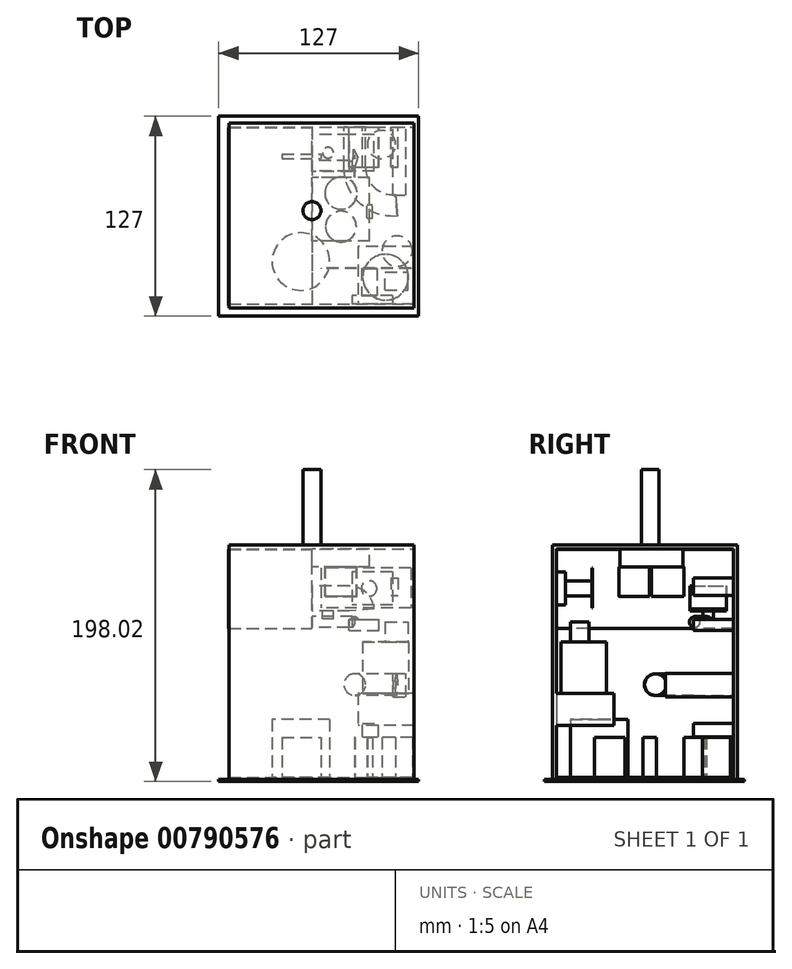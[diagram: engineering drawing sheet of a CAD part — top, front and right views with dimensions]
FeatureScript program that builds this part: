
annotation { "Feature Type Name" : "Feature", "Feature Type Description" : "" }
export const myFeature = defineFeature(function(context is Context, id is Id, definition is map)
    precondition{}
    {
        {
            var Q0;
            Q0=qCreatedBy(makeId("Top.planeOp"),FACE);
            var sketch = newSketch(context, id + "F0", { "sketchPlane" : qUnion([Q0])});
            skLineSegment(sketch, "E0.bottom", {"start": v(-58.4, 55.5) * mm, "end": v(59.1, 55.5) * mm});
            skLineSegment(sketch, "E0.top", {"start": v(-58.4, -62) * mm, "end": v(59.1, -62) * mm});
            skLineSegment(sketch, "E0.left", {"start": v(-58.4, 55.5) * mm, "end": v(-58.4, -62) * mm});
            skLineSegment(sketch, "E0.right", {"start": v(59.1, 55.5) * mm, "end": v(59.1, -62) * mm});
            skSolve(sketch);
        }
        {
            var Q0;
            Q0 = qSketchRegion(id + "F0", true);
            extrude(context, id + "F1", {"entities" : qUnion([Q0]), "depth" : 150 * mm, "offsetDistance" : 25.4 * mm});
        }
        {
            var Q0;
            Q0=makeQuery(id+"F1.opExtrude","SWEPT_FACE",FACE,{"disambiguationData":[OSD([sQuery(id+"F0.wireOp",EDGE,"E0.right")])]});
            shell(context, id + "F2", {"entities" : qUnion([Q0]), "thickness" : 2.54 * mm});
        }
        {
            var Q0;
            {var subQ0=sQuery(id+"F0.wireOp",EDGE,"E0.right");var subQ1=sQuery(id+"F0.wireOp",EDGE,"E0.left");var subQ2=sQuery(id+"F0.wireOp",EDGE,"E0.top");var subQ3=sQuery(id+"F0.wireOp",EDGE,"E0.bottom");Q0=makeQuery(id+"F2.opShell","OFFSET_FACE",FACE,{"disambiguationData":[OSD([subQ3,subQ2,subQ1,subQ0]),TDD([makeQuery(id+"F1.opExtrude","CAP_FACE",FACE,{"disambiguationData":[OSD([subQ3,subQ2,subQ1,subQ0])],"isStart":true})])]});}
            var sketch = newSketch(context, id + "F3", { "sketchPlane" : qUnion([Q0])});
            skCircle(sketch, "E1", {"center": v(-12.8, -32.36) * mm, "radius": 18.28 * mm});
            skPoint(sketch, "E1.first.point", {"position": v(-19.67, -49.3) * mm});
            skPoint(sketch, "E1.second.point", {"position": v(-30.56, -28.03) * mm});
            skPoint(sketch, "E1.third.point", {"position": v(5.48, -31.87) * mm});
            skSolve(sketch);
        }
        {
            var Q0;
            Q0 = qSketchRegion(id + "F3", true);
            extrude(context, id + "F4", {"entities" : qUnion([Q0]), "operationType" : NewBodyOperationType.ADD, "depth" : 36.83 * mm, "offsetDistance" : 25.4 * mm});
        }
        {
            var Q0;
            Q0=makeQuery(id+"F1.opExtrude","SWEPT_FACE",FACE,{"disambiguationData":[OSD([sQuery(id+"F0.wireOp",EDGE,"E0.left")])]});
            var Q1;
            Q1=makeQuery(id+"F2.opShell","OFFSET_FACE",FACE,{"disambiguationData":[OSD([sQuery(id+"F0.wireOp",EDGE,"E0.left")])]});
            var Q2;
            Q2=makeQuery(id+"F1.opExtrude","SWEPT_FACE",FACE,{"disambiguationData":[OSD([sQuery(id+"F0.wireOp",EDGE,"E0.right")])]});
            var Q3;
            Q3=makeQuery(id+"F2.opShell","OFFSET_FACE",FACE,{"disambiguationData":[OSD([sQuery(id+"F0.wireOp",EDGE,"E0.bottom")])]});
            shell(context, id + "F5", {"entities" : qUnion([Q0, Q1, Q2, Q3]), "thickness" : 2.54 * mm});
        }
        {
            var Q0;
            Q0=makeQuery(id+"F5.opShell","OFFSET_FACE",FACE,{"disambiguationData":[OSD([sQuery(id+"F0.wireOp",EDGE,"E0.top")])]});
            var sketch = newSketch(context, id + "F6", { "sketchPlane" : qUnion([Q0])});
            skLineSegment(sketch, "E2.bottom", {"start": v(-59.1, 55.93) * mm, "end": v(-23.54, 55.93) * mm});
            skLineSegment(sketch, "E2.top", {"start": v(-59.1, 35.45) * mm, "end": v(-23.54, 35.45) * mm});
            skLineSegment(sketch, "E2.left", {"start": v(-59.1, 55.93) * mm, "end": v(-59.1, 35.45) * mm});
            skLineSegment(sketch, "E2.right", {"start": v(-23.54, 55.93) * mm, "end": v(-23.54, 35.45) * mm});
            skSolve(sketch);
        }
        {
            var Q0;
            Q0 = qSketchRegion(id + "F6", true);
            extrude(context, id + "F7", {"entities" : qUnion([Q0]), "operationType" : NewBodyOperationType.ADD, "depth" : 36.58 * mm, "offsetDistance" : 25.4 * mm});
        }
        {
            var Q0;
            Q0=makeQuery(id+"F7.opExtrude","SWEPT_FACE",FACE,{"disambiguationData":[OSD([sQuery(id+"F6.wireOp",EDGE,"E2.bottom")])]});
            var sketch = newSketch(context, id + "F8", { "sketchPlane" : qUnion([Q0])});
            skCircle(sketch, "E3", {"center": v(41.03, -42.29) * mm, "radius": 14.54 * mm});
            skSolve(sketch);
        }
        {
            var Q0;
            Q0 = qSketchRegion(id + "F8", true);
            extrude(context, id + "F9", {"entities" : qUnion([Q0]), "operationType" : NewBodyOperationType.ADD, "depth" : 32.77 * mm, "offsetDistance" : 25.4 * mm});
        }
        {
            var Q0;
            Q0=makeQuery(id+"F9.opExtrude","CAP_FACE",FACE,{"disambiguationData":[OSD([sQuery(id+"F8.wireOp",EDGE,"E3")])],"isStart":false});
            var sketch = newSketch(context, id + "F10", { "sketchPlane" : qUnion([Q0])});
            skLineSegment(sketch, "E4.bottom", {"start": v(40.7, -50.53) * mm, "end": v(55.2, -50.53) * mm});
            skLineSegment(sketch, "E4.top", {"start": v(40.7, -39.02) * mm, "end": v(55.2, -39.02) * mm});
            skLineSegment(sketch, "E4.left", {"start": v(40.7, -50.53) * mm, "end": v(40.7, -39.02) * mm});
            skLineSegment(sketch, "E4.right", {"start": v(55.2, -50.53) * mm, "end": v(55.2, -39.02) * mm});
            skSolve(sketch);
        }
        {
            var Q0;
            Q0 = qSketchRegion(id + "F10", true);
            extrude(context, id + "F11", {"entities" : qUnion([Q0]), "operationType" : NewBodyOperationType.ADD, "depth" : 12.45 * mm, "offsetDistance" : 25.4 * mm});
        }
        {
            var Q0;
            Q0=makeQuery(id+"F5.opShell","OFFSET_FACE",FACE,{"disambiguationData":[OSD([sQuery(id+"F0.wireOp",EDGE,"E0.top")])]});
            var sketch = newSketch(context, id + "F12", { "sketchPlane" : qUnion([Q0])});
            skLineSegment(sketch, "E5.bottom", {"start": v(-45.48, 133) * mm, "end": v(-19.63, 133) * mm});
            skLineSegment(sketch, "E5.top", {"start": v(-45.48, 112.07) * mm, "end": v(-19.63, 112.07) * mm});
            skLineSegment(sketch, "E5.left", {"start": v(-45.48, 133) * mm, "end": v(-45.48, 112.07) * mm});
            skLineSegment(sketch, "E5.right", {"start": v(-19.63, 133) * mm, "end": v(-19.63, 112.07) * mm});
            skSolve(sketch);
        }
        {
            var Q0;
            Q0 = qSketchRegion(id + "F12", true);
            extrude(context, id + "F13", {"entities" : qUnion([Q0]), "operationType" : NewBodyOperationType.ADD, "depth" : 5.6 * mm, "offsetDistance" : 25.4 * mm});
        }
        {
            var Q0;
            Q0=makeQuery(id+"F13.opExtrude","CAP_FACE",FACE,{"disambiguationData":[OSD([sQuery(id+"F12.wireOp",EDGE,"E5.bottom"),sQuery(id+"F12.wireOp",EDGE,"E5.top"),sQuery(id+"F12.wireOp",EDGE,"E5.left"),sQuery(id+"F12.wireOp",EDGE,"E5.right")])],"isStart":false});
            var sketch = newSketch(context, id + "F14", { "sketchPlane" : qUnion([Q0])});
            skCircle(sketch, "E6", {"center": v(-30.58, 122.53) * mm, "radius": 4.9 * mm});
            skPoint(sketch, "E6.centerSnap0", {"position": v(-45.48, 122.53) * mm});
            skSolve(sketch);
        }
        {
            var Q0;
            Q0 = qSketchRegion(id + "F14", true);
            extrude(context, id + "F15", {"entities" : qUnion([Q0]), "operationType" : NewBodyOperationType.ADD, "depth" : 17.02 * mm, "offsetDistance" : 25.4 * mm});
        }
        {
            var Q0;
            Q0=makeQuery(id+"F15.opExtrude","CAP_FACE",FACE,{"disambiguationData":[OSD([sQuery(id+"F14.wireOp",EDGE,"E6")])],"isStart":false});
            var sketch = newSketch(context, id + "F16", { "sketchPlane" : qUnion([Q0])});
            skLineSegment(sketch, "E7.bottom", {"start": v(-57.13, 135.48) * mm, "end": v(0, 135.48) * mm});
            skLineSegment(sketch, "E7.top", {"start": v(-57.13, 110) * mm, "end": v(0, 110) * mm});
            skLineSegment(sketch, "E7.left", {"start": v(-57.13, 135.48) * mm, "end": v(-57.13, 110) * mm});
            skLineSegment(sketch, "E7.right", {"start": v(0, 135.48) * mm, "end": v(0, 110) * mm});
            skSolve(sketch);
        }
        {
            var Q0;
            Q0 = qSketchRegion(id + "F16", true);
            extrude(context, id + "F17", {"entities" : qUnion([Q0]), "operationType" : NewBodyOperationType.ADD, "depth" : 0.25 * mm, "offsetDistance" : 25.4 * mm});
        }
        {
            var Q0;
            {var subQ0=sQuery(id+"F0.wireOp",EDGE,"E0.right");var subQ1=sQuery(id+"F0.wireOp",EDGE,"E0.left");var subQ2=sQuery(id+"F0.wireOp",EDGE,"E0.top");var subQ3=sQuery(id+"F0.wireOp",EDGE,"E0.bottom");var subQ4=makeQuery(id+"F1.opExtrude","CAP_FACE",FACE,{"disambiguationData":[OSD([subQ3,subQ2,subQ1,subQ0])],"isStart":false});Q0=makeQuery(id+"F5.opShell","OFFSET_FACE",FACE,{"disambiguationData":[OSD([subQ3,subQ2,subQ1,subQ0]),TDD([subQ4,makeQuery(id+"F2.opShell","OFFSET_FACE",FACE,{"disambiguationData":[OSD([subQ3,subQ2,subQ1,subQ0]),TDD([subQ4])]})])]});}
            var sketch = newSketch(context, id + "F18", { "sketchPlane" : qUnion([Q0])});
            skLineSegment(sketch, "E8.bottom", {"start": v(30.96, 19.28) * mm, "end": v(-5.57, 19.28) * mm});
            skLineSegment(sketch, "E8.top", {"start": v(30.96, -20.92) * mm, "end": v(-5.57, -20.92) * mm});
            skLineSegment(sketch, "E8.left", {"start": v(30.96, 19.28) * mm, "end": v(30.96, -20.92) * mm});
            skLineSegment(sketch, "E8.right", {"start": v(-5.57, 19.28) * mm, "end": v(-5.57, -20.92) * mm});
            skSolve(sketch);
        }
        {
            var Q0;
            Q0 = qSketchRegion(id + "F18", true);
            extrude(context, id + "F19", {"entities" : qUnion([Q0]), "operationType" : NewBodyOperationType.ADD, "depth" : 11.18 * mm, "offsetDistance" : 25.4 * mm});
        }
        {
            var Q0;
            Q0=makeQuery(id+"F19.opExtrude","CAP_FACE",FACE,{"disambiguationData":[OSD([sQuery(id+"F18.wireOp",EDGE,"E8.bottom"),sQuery(id+"F18.wireOp",EDGE,"E8.top"),sQuery(id+"F18.wireOp",EDGE,"E8.left"),sQuery(id+"F18.wireOp",EDGE,"E8.right")])],"isStart":false});
            var sketch = newSketch(context, id + "F20", { "sketchPlane" : qUnion([Q0])});
            skCircle(sketch, "E9", {"center": v(12.7, 10.12) * mm, "radius": 9.76 * mm});
            skPoint(sketch, "E9.centerSnap0", {"position": v(12.7, 19.28) * mm});
            skCircle(sketch, "E10", {"center": v(12.7, -11.06) * mm, "radius": 10.22 * mm});
            skSolve(sketch);
        }
        {
            var Q0;
            Q0 = qSketchRegion(id + "F20", true);
            extrude(context, id + "F21", {"entities" : qUnion([Q0]), "operationType" : NewBodyOperationType.ADD, "depth" : 18.8 * mm, "offsetDistance" : 25.4 * mm});
        }
        {
            var Q0;
            Q0=makeQuery(id+"F19.opExtrude","SWEPT_FACE",FACE,{"disambiguationData":[OSD([sQuery(id+"F18.wireOp",EDGE,"E8.right")])]});
            var sketch = newSketch(context, id + "F22", { "sketchPlane" : qUnion([Q0])});
            skLineSegment(sketch, "E11.bottom", {"start": v(-52.73, 147.3) * mm, "end": v(60.28, 147.3) * mm});
            skLineSegment(sketch, "E11.top", {"start": v(-52.73, 97.03) * mm, "end": v(60.28, 97.03) * mm});
            skLineSegment(sketch, "E11.left", {"start": v(-52.73, 147.3) * mm, "end": v(-52.73, 97.03) * mm});
            skLineSegment(sketch, "E11.right", {"start": v(60.28, 147.3) * mm, "end": v(60.28, 97.03) * mm});
            skSolve(sketch);
        }
        {
            var Q0;
            Q0 = qSketchRegion(id + "F22", true);
            extrude(context, id + "F23", {"entities" : qUnion([Q0]), "operationType" : NewBodyOperationType.ADD, "depth" : 53.1 * mm, "offsetDistance" : 25.4 * mm});
        }
        {
            var Q0;
            Q0=makeQuery(id+"F23.opExtrude","CAP_FACE",FACE,{"disambiguationData":[OSD([sQuery(id+"F22.wireOp",EDGE,"E11.bottom"),sQuery(id+"F22.wireOp",EDGE,"E11.top"),sQuery(id+"F22.wireOp",EDGE,"E11.left"),sQuery(id+"F22.wireOp",EDGE,"E11.right")])],"isStart":true});
            var sketch = newSketch(context, id + "F24", { "sketchPlane" : qUnion([Q0])});
            skLineSegment(sketch, "E12.bottom", {"start": v(25.13, 123.97) * mm, "end": v(48.46, 123.97) * mm});
            skLineSegment(sketch, "E12.top", {"start": v(25.13, 108.2) * mm, "end": v(48.46, 108.2) * mm});
            skLineSegment(sketch, "E12.left", {"start": v(25.13, 123.97) * mm, "end": v(25.13, 108.2) * mm});
            skLineSegment(sketch, "E12.right", {"start": v(48.46, 123.97) * mm, "end": v(48.46, 108.2) * mm});
            skSolve(sketch);
        }
        {
            var Q0;
            Q0 = qSketchRegion(id + "F24", true);
            extrude(context, id + "F25", {"entities" : qUnion([Q0]), "operationType" : NewBodyOperationType.ADD, "depth" : 23.62 * mm, "offsetDistance" : 25.4 * mm});
        }
        {
            var Q0;
            Q0=makeQuery(id+"F25.opExtrude","CAP_FACE",FACE,{"disambiguationData":[OSD([sQuery(id+"F24.wireOp",EDGE,"E12.bottom"),sQuery(id+"F24.wireOp",EDGE,"E12.top"),sQuery(id+"F24.wireOp",EDGE,"E12.left"),sQuery(id+"F24.wireOp",EDGE,"E12.right")])],"isStart":false});
            var Q1;
            Q1=makeQuery(id+"F25.opExtrude","CAP_EDGE",EDGE,{"disambiguationData":[OSD([sQuery(id+"F24.wireOp",EDGE,"E12.top")])],"isStart":false});
            revolve(context, id + "F26", {"operationType" : NewBodyOperationType.ADD, "surfaceOperationType" : NewSurfaceOperationType.NEW, "entities" : qUnion([Q0]), "axis" : qUnion([Q1]), "revolveType" : RevolveType.ONE_DIRECTION, "angle" : 85 * degree});
        }
        {
            var Q0;
            Q0=makeQuery(id+"F23.opExtrude","CAP_FACE",FACE,{"disambiguationData":[OSD([sQuery(id+"F22.wireOp",EDGE,"E11.bottom"),sQuery(id+"F22.wireOp",EDGE,"E11.top"),sQuery(id+"F22.wireOp",EDGE,"E11.left"),sQuery(id+"F22.wireOp",EDGE,"E11.right")])],"isStart":true});
            var sketch = newSketch(context, id + "F27", { "sketchPlane" : qUnion([Q0])});
            skCircle(sketch, "E13", {"center": v(28.27, 101.2) * mm, "radius": 3.4 * mm});
            skSolve(sketch);
        }
        {
            var Q0;
            Q0 = qSketchRegion(id + "F27", true);
            extrude(context, id + "F28", {"entities" : qUnion([Q0]), "operationType" : NewBodyOperationType.ADD, "depth" : 25.4 * mm, "offsetDistance" : 25.4 * mm});
        }
        {
            var Q0;
            Q0=makeQuery(id+"F25.opExtrude","SWEPT_FACE",FACE,{"disambiguationData":[OSD([sQuery(id+"F24.wireOp",EDGE,"E12.top")])]});
            var sketch = newSketch(context, id + "F29", { "sketchPlane" : qUnion([Q0])});
            skCircle(sketch, "E14", {"center": v(4.46, -36.8) * mm, "radius": 3.44 * mm});
            skPoint(sketch, "E14.centerSnap0", {"position": v(18.05, -36.8) * mm});
            skSolve(sketch);
        }
        {
            var Q0;
            Q0 = qSketchRegion(id + "F29", true);
            extrude(context, id + "F30", {"entities" : qUnion([Q0]), "operationType" : NewBodyOperationType.ADD, "depth" : 5.08 * mm, "offsetDistance" : 25.4 * mm});
        }
        {
            var Q0;
            Q0=makeQuery(id+"F28.opExtrude","CAP_FACE",FACE,{"disambiguationData":[OSD([sQuery(id+"F27.wireOp",EDGE,"E13")])],"isStart":false});
            var Q1;
            Q1=makeQuery(id+"F30.opExtrude","CAP_EDGE",EDGE,{"disambiguationData":[OSD([sQuery(id+"F29.wireOp",EDGE,"E14")])],"isStart":false});
            revolve(context, id + "F31", {"operationType" : NewBodyOperationType.ADD, "surfaceOperationType" : NewSurfaceOperationType.NEW, "entities" : qUnion([Q0]), "axis" : qUnion([Q1]), "revolveType" : RevolveType.ONE_DIRECTION, "oppositeDirection" : true, "angle" : 27.4 * degree});
        }
        {
            var Q0;
            Q0=makeQuery(id+"F5.opShell","OFFSET_FACE",FACE,{"disambiguationData":[OSD([sQuery(id+"F0.wireOp",EDGE,"E0.bottom")])]});
            var sketch = newSketch(context, id + "F32", { "sketchPlane" : qUnion([Q0])});
            skLineSegment(sketch, "E15.bottom", {"start": v(17.78, 95.9) * mm, "end": v(36.86, 95.9) * mm});
            skLineSegment(sketch, "E15.top", {"start": v(17.78, 102.8) * mm, "end": v(36.86, 102.8) * mm});
            skLineSegment(sketch, "E15.left", {"start": v(17.78, 95.9) * mm, "end": v(17.78, 102.8) * mm});
            skLineSegment(sketch, "E15.right", {"start": v(36.86, 95.9) * mm, "end": v(36.86, 102.8) * mm});
            skLineSegment(sketch, "E16.bottom", {"start": v(26.47, 28.3) * mm, "end": v(36.7, 28.3) * mm});
            skLineSegment(sketch, "E16.top", {"start": v(26.47, 36.83) * mm, "end": v(36.7, 36.83) * mm});
            skLineSegment(sketch, "E16.left", {"start": v(26.47, 28.3) * mm, "end": v(26.47, 36.83) * mm});
            skLineSegment(sketch, "E16.right", {"start": v(36.7, 28.3) * mm, "end": v(36.7, 36.83) * mm});
            skCircle(sketch, "E17", {"center": v(21.48, 61.44) * mm, "radius": 6.87 * mm});
            skLineSegment(sketch, "E18.bottom", {"start": v(44.46, 129.34) * mm, "end": v(48.91, 129.34) * mm});
            skLineSegment(sketch, "E18.top", {"start": v(44.46, 118.2) * mm, "end": v(48.91, 118.2) * mm});
            skLineSegment(sketch, "E18.left", {"start": v(44.46, 129.34) * mm, "end": v(44.46, 118.2) * mm});
            skLineSegment(sketch, "E18.right", {"start": v(48.91, 129.34) * mm, "end": v(48.91, 118.2) * mm});
            skLineSegment(sketch, "E19.bottom", {"start": v(45.82, 53.53) * mm, "end": v(53.9, 53.53) * mm});
            skLineSegment(sketch, "E19.top", {"start": v(45.82, 68.67) * mm, "end": v(53.9, 68.67) * mm});
            skLineSegment(sketch, "E19.left", {"start": v(45.82, 53.53) * mm, "end": v(45.82, 68.67) * mm});
            skLineSegment(sketch, "E19.right", {"start": v(53.9, 53.53) * mm, "end": v(53.9, 68.67) * mm});
            skSolve(sketch);
        }
        {
            var Q0;
            Q0 = qSketchRegion(id + "F32", true);
            extrude(context, id + "F33", {"entities" : qUnion([Q0]), "operationType" : NewBodyOperationType.ADD, "depth" : 25.4 * mm, "offsetDistance" : 25.4 * mm});
        }
        {
            var Q0;
            Q0=makeQuery(id+"F33.opExtrude","CAP_FACE",FACE,{"disambiguationData":[OSD([sQuery(id+"F32.wireOp",EDGE,"E17")])],"isStart":false});
            var Q1;
            Q1=makeQuery(id+"F33.opExtrude","CAP_EDGE",EDGE,{"disambiguationData":[OSD([sQuery(id+"F32.wireOp",EDGE,"E19.left")])],"isStart":false});
            revolve(context, id + "F34", {"operationType" : NewBodyOperationType.ADD, "surfaceOperationType" : NewSurfaceOperationType.NEW, "entities" : qUnion([Q0]), "axis" : qUnion([Q1]), "revolveType" : RevolveType.ONE_DIRECTION, "angle" : 95 * degree});
        }
        {
            var Q0;
            Q0=makeQuery(id+"F33.opExtrude","CAP_FACE",FACE,{"disambiguationData":[OSD([sQuery(id+"F32.wireOp",EDGE,"E19.bottom"),sQuery(id+"F32.wireOp",EDGE,"E19.top"),sQuery(id+"F32.wireOp",EDGE,"E19.left"),sQuery(id+"F32.wireOp",EDGE,"E19.right")])],"isStart":false});
            extrude(context, id + "F35", {"entities" : qUnion([Q0]), "operationType" : NewBodyOperationType.ADD, "depth" : 17.78 * mm, "offsetDistance" : 25.4 * mm});
        }
        {
            var Q0;
            {var subQ0=sQuery(id+"F0.wireOp",EDGE,"E0.right");var subQ1=sQuery(id+"F0.wireOp",EDGE,"E0.left");var subQ2=sQuery(id+"F0.wireOp",EDGE,"E0.top");var subQ3=sQuery(id+"F0.wireOp",EDGE,"E0.bottom");var subQ4=makeQuery(id+"F1.opExtrude","CAP_FACE",FACE,{"disambiguationData":[OSD([subQ3,subQ2,subQ1,subQ0])],"isStart":true});Q0=makeQuery(id+"F5.opShell","OFFSET_FACE",FACE,{"disambiguationData":[OSD([subQ3,subQ2,subQ1,subQ0]),TDD([subQ4,makeQuery(id+"F2.opShell","OFFSET_FACE",FACE,{"disambiguationData":[OSD([subQ3,subQ2,subQ1,subQ0]),TDD([subQ4])]})])]});}
            var sketch = newSketch(context, id + "F36", { "sketchPlane" : qUnion([Q0])});
            skCircle(sketch, "E20", {"center": v(48.4, -25.67) * mm, "radius": 9.66 * mm});
            skLineSegment(sketch, "E21.bottom", {"start": v(29.15, -4.61) * mm, "end": v(32.6, -4.61) * mm});
            skLineSegment(sketch, "E21.top", {"start": v(29.15, 3.96) * mm, "end": v(32.6, 3.96) * mm});
            skLineSegment(sketch, "E21.left", {"start": v(29.15, -4.61) * mm, "end": v(29.15, 3.96) * mm});
            skLineSegment(sketch, "E21.right", {"start": v(32.6, -4.61) * mm, "end": v(32.6, 3.96) * mm});
            skLineSegment(sketch, "E22.bottom", {"start": v(-24.6, 35.78) * mm, "end": v(0, 35.78) * mm});
            skLineSegment(sketch, "E22.top", {"start": v(-24.6, 33.11) * mm, "end": v(0, 33.11) * mm});
            skLineSegment(sketch, "E22.left", {"start": v(-24.6, 35.78) * mm, "end": v(-24.6, 33.11) * mm});
            skLineSegment(sketch, "E22.right", {"start": v(0, 35.78) * mm, "end": v(0, 33.11) * mm});
            skLineSegment(sketch, "E23.bottom", {"start": v(21.6, 21.4) * mm, "end": v(21.23, 21.4) * mm});
            skLineSegment(sketch, "E23.top", {"start": v(21.6, 34.76) * mm, "end": v(21.23, 34.76) * mm});
            skLineSegment(sketch, "E23.left", {"start": v(21.6, 21.4) * mm, "end": v(21.6, 34.76) * mm});
            skLineSegment(sketch, "E23.right", {"start": v(21.23, 21.4) * mm, "end": v(21.23, 34.76) * mm});
            skCircle(sketch, "E24", {"center": v(38.47, 42.04) * mm, "radius": 8.93 * mm});
            skArc(sketch, "E25", {"start": v(36.14, 12.02) * mm, "mid": v(41.99, 5.4) * mm, "end": v(50.39, 8.13) * mm});
            skArc(sketch, "E26", {"start": v(25.26, -40.13) * mm, "mid": v(27.9, -47.49) * mm, "end": v(35.02, -44.23) * mm});
            skSolve(sketch);
        }
        {
            var Q0;
            Q0 = qSketchRegion(id + "F36", true);
            extrude(context, id + "F37", {"entities" : qUnion([Q0]), "operationType" : NewBodyOperationType.ADD, "depth" : 25.4 * mm, "offsetDistance" : 25.4 * mm});
        }
        {
            var Q0;
            Q0=makeQuery(id+"F1.opExtrude","CAP_FACE",FACE,{"disambiguationData":[OSD([sQuery(id+"F0.wireOp",EDGE,"E0.bottom"),sQuery(id+"F0.wireOp",EDGE,"E0.top"),sQuery(id+"F0.wireOp",EDGE,"E0.left"),sQuery(id+"F0.wireOp",EDGE,"E0.right")])],"isStart":false});
            var sketch = newSketch(context, id + "F38", { "sketchPlane" : qUnion([Q0])});
            skCircle(sketch, "E27", {"center": v(-5.7, 0) * mm, "radius": 5.7 * mm});
            skSolve(sketch);
        }
        {
            var Q0;
            Q0 = qSketchRegion(id + "F38", true);
            extrude(context, id + "F39", {"entities" : qUnion([Q0]), "operationType" : NewBodyOperationType.ADD, "depth" : 48 * mm, "offsetDistance" : 25.4 * mm});
        }
        {
            var Q0;
            Q0=qCreatedBy(makeId("Top.planeOp"),FACE);
            var sketch = newSketch(context, id + "F40", { "sketchPlane" : qUnion([Q0])});
            skPoint(sketch, "E28.middle", {"position": v(0, 0) * mm});
            skLineSegment(sketch, "E29.bottom", {"start": v(-64.9, -67) * mm, "end": v(62.1, -67) * mm});
            skLineSegment(sketch, "E29.top", {"start": v(-64.9, 60) * mm, "end": v(62.1, 60) * mm});
            skLineSegment(sketch, "E29.left", {"start": v(-64.9, -67) * mm, "end": v(-64.9, 60) * mm});
            skLineSegment(sketch, "E29.right", {"start": v(62.1, -67) * mm, "end": v(62.1, 60) * mm});
            skSolve(sketch);
        }
        {
            var Q0;
            Q0 = qSketchRegion(id + "F40", true);
            extrude(context, id + "F41", {"entities" : qUnion([Q0]), "operationType" : NewBodyOperationType.ADD, "depth" : 1.27 * mm, "offsetDistance" : 25.4 * mm});
        }
    });
